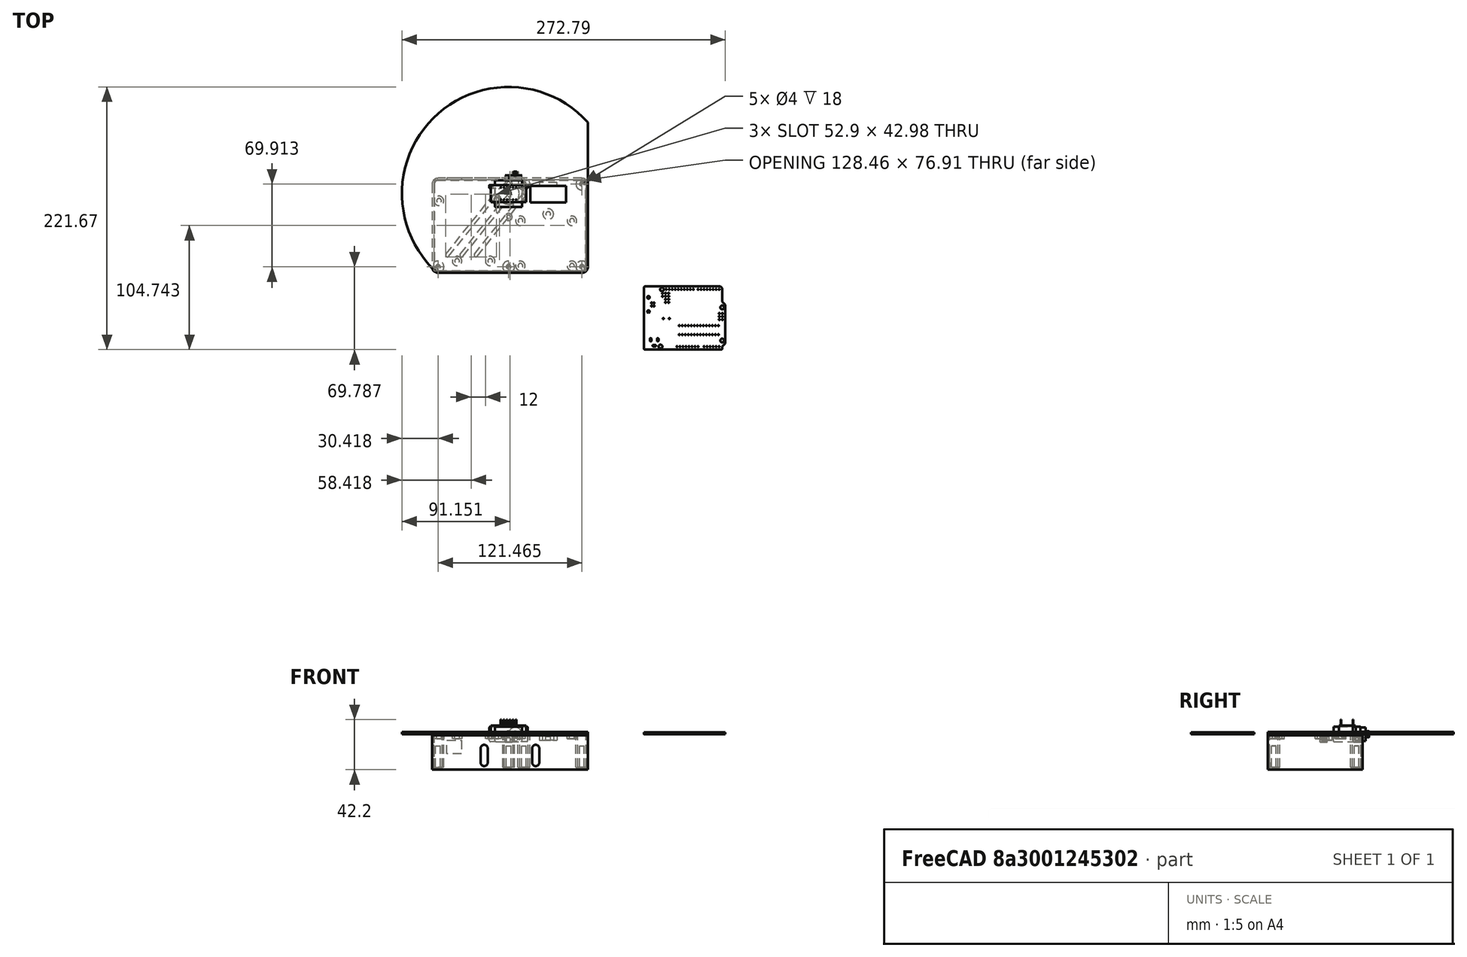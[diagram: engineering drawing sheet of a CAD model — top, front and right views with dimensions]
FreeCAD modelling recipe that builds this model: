
FCSTD DOCUMENT  (FreeCAD 1.0RUnknown)
Label: shell
License: All rights reserved
LicenseURL: https://en.wikipedia.org/wiki/All_rights_reserved
objects: Sketcher::SketchObject×12, PartDesign::Pad×9, PartDesign::Pocket×5, PartDesign::Hole×5, App::Link×4, App::FeaturePython×4, Part::Feature×3, PartDesign::SubShapeBinder×2, PartDesign::Body×2, App::Part×1, Assembly::JointGroup×1, Assembly::AssemblyObject×1, PartDesign::Chamfer×1
note: 91 computed .brp shape members not serialized (recipe doc carries the construction recipe); baked Part::Feature solids carry a one-line shape summary decoded from their .brp

FEATURE [Sketcher::SketchObject] Sketch
  ArcFitTolerance = 1e-06
  AttachmentSupport = -> [XY_Plane]
  FullyConstrained = true
  MakeInternals = false
  MapMode = 5
  sketch-geometry (14):
    g0: LineSegment StartX=18.4415 StartY=6.5 StartZ=0 EndX=18.4415 EndY=-7.5 EndZ=0
    g1: LineSegment StartX=18.4415 StartY=-7.5 StartZ=0 EndX=48.4415 EndY=-7.5 EndZ=0
    g2: LineSegment StartX=48.4415 StartY=-7.5 StartZ=0 EndX=48.4415 EndY=6.5 EndZ=0
    g3: LineSegment StartX=48.4415 StartY=6.5 StartZ=0 EndX=18.4415 EndY=6.5 EndZ=0
    g4: GeomPoint [constr] X=33.4415 Y=-0.5 Z=0
    g5: ArcOfCircle CenterX=0 CenterY=0 CenterZ=0 NormalX=0 NormalY=0 NormalZ=1 AngleXU=0 Radius=90 StartAngle=0.733038 EndAngle=3.97935
    g6: Circle CenterX=0 CenterY=0 CenterZ=0 NormalX=0 NormalY=0 NormalZ=1 AngleXU=0 Radius=2.5
    g7: LineSegment [constr] StartX=0 StartY=0 StartZ=0 EndX=66.883 EndY=60.2218 EndZ=0
    g8: LineSegment [constr] StartX=0 StartY=0 StartZ=0 EndX=-60.2218 EndY=-66.883 EndZ=0
    g9: LineSegment StartX=66.883 StartY=60.2218 StartZ=0 EndX=66.883 EndY=-61.883 EndZ=0
    g10: LineSegment StartX=61.883 StartY=-66.883 StartZ=0 EndX=-60.2218 EndY=-66.883 EndZ=0
    g11: ArcOfCircle CenterX=61.883 CenterY=-61.883 CenterZ=0 NormalX=0 NormalY=0 NormalZ=1 AngleXU=0 Radius=5 StartAngle=4.71239 EndAngle=6.28319
    g12: LineSegment [constr] StartX=48.4415 StartY=3.78 StartZ=0 EndX=66.883 EndY=3.78 EndZ=0
    g13: LineSegment [constr] StartX=0 StartY=0 StartZ=0 EndX=18.4415 EndY=0 EndZ=0
  constraints (37):
    c: Coincident(g0,g1)
    c: Coincident(g1,g2)
    c: Coincident(g2,g3)
    c: Coincident(g3,g0)
    c: Vertical(g2)
    c: Horizontal(g1)
    c: Horizontal(g3)
    c: Symmetric(g2,g0,g4)
    c: DistanceX(g1,g1) = 30
    c: DistanceY(g2,g2) = 14
    c: Radius(g5) = 90
    c: Coincident(g5,g-1)
    c: Coincident(g6,g5)
    c: Diameter(g6) = 5
    c: Coincident(g7,g5)
    c: Coincident(g8,g5)
    c: Angle(g8,g-1,g5) = 2.30383
    c: Vertical(g9)
    c: Horizontal(g10)
    c: Angle(g-1,g7) = 0.733038
    c: Tangent(g9,g11) = 1.5708
    c: Tangent(g10,g11) = 1.5708
    c: Radius(g11) = 5
    c: Coincident(g5,g8)
    c: Coincident(g5,g7)
    c: Coincident(g9,g5)
    c: Coincident(g10,g5)
    c: PointOnObject(g12,g9)
    c: PointOnObject(g12,g2)
    c: DistanceY(g-1,g12) = 3.78
    c: Horizontal(g12,g12)
    c: Coincident(g13,g5)
    c: Vertical(g13,g0)
    c: PointOnObject(g13,g-1)
    c: Equal(g12,g13)
    c: Perpendicular(g0,g1)
    c: DistanceY(g-1,g4) = -0.5
FEATURE [PartDesign::Pad] Pad  label="BaseFace"
  Direction = (0,0,1)
  Length = 2
  Length2 = 10
  Profile = -> Sketch
  ReferenceAxis = -> Sketch [N_Axis]
  Refine = true
  Suppressed = false
  Type = 0
FEATURE [Sketcher::SketchObject] Sketch001
  ArcFitTolerance = 1e-06
  AttachmentSupport = -> [XY_Plane]
  FullyConstrained = true
  MakeInternals = false
  MapMode = 2
  sketch-geometry (1):
    g0: Circle CenterX=0 CenterY=0 CenterZ=0 NormalX=0 NormalY=0 NormalZ=1 AngleXU=0 Radius=9
  constraints (2):
    c: Diameter(g0) = 18
    c: Coincident(g0,g-1)
FEATURE [Sketcher::SketchObject] Sketch003
  ArcFitTolerance = 1e-06
  AttachmentOffset = pos=(0,0,2) rot=(0,0,1;0rad)
  AttachmentSupport = -> [XY_Plane]
  FullyConstrained = true
  MakeInternals = false
  MapMode = 5
  Placement = pos=(0,0,2) rot=(0,0,1;0rad)
  expr: .AttachmentOffset.Base.z = <<BaseFace>>.Length
  sketch-geometry (3):
    g0: Circle CenterX=0 CenterY=-19.72 CenterZ=0 NormalX=0 NormalY=0 NormalZ=1 AngleXU=0 Radius=3
    g1: Circle CenterX=0 CenterY=8.53 CenterZ=0 NormalX=0 NormalY=0 NormalZ=1 AngleXU=0 Radius=3
    g2: LineSegment [constr] StartX=0 StartY=-19.72 StartZ=0 EndX=0 EndY=8.53 EndZ=0
  constraints (8):
    c: Diameter(g0) = 6
    c: Diameter(g1) = 6
    c: Distance(g0,g1) = 28.25
    c: Distance(g1,g-1) = 8.53
    c: Coincident(g2,g0)
    c: Coincident(g2,g1)
    c: PointOnObject(g-1,g2)
    c: PointOnObject(g0,g-2)
FEATURE [PartDesign::Pocket] Pocket001  label="PocketServo"
  BaseFeature = -> Pad
  Direction = (0,0,-1)
  Length = 1.5
  Length2 = 5
  Profile = -> Sketch001
  ReferenceAxis = -> Sketch001 [N_Axis]
  Refine = true
  Reversed = true
  Suppressed = false
  Type = 0
FEATURE [Sketcher::SketchObject] Sketch002
  ArcFitTolerance = 1e-06
  AttachmentSupport = -> [XY_Plane]
  ExternalGeometry = -> [Pocket001]
  FullyConstrained = true
  MakeInternals = false
  MapMode = 5
  sketch-geometry (5):
    g0: Circle CenterX=-43.4418 CenterY=-56.923 CenterZ=0 NormalX=0 NormalY=0 NormalZ=1 AngleXU=0 Radius=4
    g1: Circle CenterX=-15.5018 CenterY=-56.923 CenterZ=0 NormalX=0 NormalY=0 NormalZ=1 AngleXU=0 Radius=4
    g2: Circle CenterX=-10.4218 CenterY=-4.85303 CenterZ=0 NormalX=0 NormalY=0 NormalZ=1 AngleXU=0 Radius=4
    g3: Circle CenterX=-58.6818 CenterY=-6.12303 CenterZ=0 NormalX=0 NormalY=0 NormalZ=1 AngleXU=0 Radius=4
    g4: GeomPoint X=-61.2218 Y=9.11697 Z=0
  constraints (14):
    c: Equal(g1,g0)
    c: Equal(g0,g3)
    c: Equal(g3,g2)
    c: Diameter(g3) = 8
    c: DistanceY(g4,g3) = -15.24
    c: DistanceY(g4,g0) = -66.04
    c: Horizontal(g0,g1)
    c: DistanceX(g4,g3) = 2.54
    c: DistanceX(g4,g2) = 50.8
    c: DistanceX(g4,g0) = 17.78
    c: DistanceX(g4,g1) = 45.72
    c: DistanceX(g4,g-3) = 1
    c: DistanceY(g4,g-3) = -76
    c: DistanceY(g4,g2) = -13.97
FEATURE [PartDesign::Pad] Pad005  label="PadArduino"
  BaseFeature = -> Pocket001
  Direction = (0,0,1)
  Length = 4
  Length2 = 10
  Profile = -> Sketch002
  ReferenceAxis = -> Sketch002 [N_Axis]
  Refine = true
  Reversed = true
  Suppressed = false
  Type = 0
FEATURE [PartDesign::Pad] Pad002  label="PadServo"
  BaseFeature = -> Pad005
  Direction = (0,0,1)
  Length = 8.75
  Length2 = 10
  Profile = -> Sketch003
  ReferenceAxis = -> Sketch003 [N_Axis]
  Refine = true
  Reversed = true
  Suppressed = false
  Type = 0
  expr: Length = 6.75 mm + <<BaseFace>>.Length
FEATURE [Sketcher::SketchObject] Sketch004
  ArcFitTolerance = 1e-06
  AttachmentSupport = -> [XY_Plane003]
  ExternalGeometry = -> [Pad002]
  FullyConstrained = true
  MakeInternals = false
  MapMode = 5
  sketch-geometry (16):
    g0: LineSegment StartX=61.883 StartY=11.53 StartZ=0 EndX=-59.5818 EndY=11.53 EndZ=0
    g1: LineSegment StartX=-63.0818 StartY=8.03 StartZ=0 EndX=-63.0818 EndY=-61.883 EndZ=0
    g2: LineSegment StartX=-59.5818 StartY=-65.383 StartZ=0 EndX=61.883 EndY=-65.383 EndZ=0
    g3: LineSegment StartX=65.383 StartY=-61.883 StartZ=0 EndX=65.383 EndY=8.03 EndZ=0
    g4: ArcOfCircle CenterX=61.883 CenterY=8.03 CenterZ=0 NormalX=0 NormalY=0 NormalZ=1 AngleXU=0 Radius=3.5 StartAngle=1e-16 EndAngle=1.5708
    g5: ArcOfCircle CenterX=-59.5818 CenterY=8.03 CenterZ=0 NormalX=0 NormalY=0 NormalZ=1 AngleXU=0 Radius=3.5 StartAngle=1.5708 EndAngle=3.14159
    g6: ArcOfCircle CenterX=-59.5818 CenterY=-61.883 CenterZ=0 NormalX=0 NormalY=0 NormalZ=1 AngleXU=0 Radius=3.5 StartAngle=3.14159 EndAngle=4.71239
    g7: ArcOfCircle CenterX=61.883 CenterY=-61.883 CenterZ=0 NormalX=0 NormalY=0 NormalZ=1 AngleXU=0 Radius=3.5 StartAngle=4.71239 EndAngle=6.28319
    g8: LineSegment StartX=61.883 StartY=13.03 StartZ=0 EndX=-59.5818 EndY=13.03 EndZ=0
    g9: LineSegment StartX=-64.5818 StartY=8.03 StartZ=0 EndX=-64.5818 EndY=-61.883 EndZ=0
    g10: LineSegment StartX=-59.5818 StartY=-66.883 StartZ=0 EndX=61.883 EndY=-66.883 EndZ=0
    g11: LineSegment StartX=66.883 StartY=-61.883 StartZ=0 EndX=66.883 EndY=8.03 EndZ=0
    g12: ArcOfCircle CenterX=61.883 CenterY=8.03 CenterZ=0 NormalX=0 NormalY=0 NormalZ=1 AngleXU=0 Radius=5 StartAngle=0 EndAngle=1.5708
    g13: ArcOfCircle CenterX=-59.5818 CenterY=8.03 CenterZ=0 NormalX=0 NormalY=0 NormalZ=1 AngleXU=0 Radius=5 StartAngle=1.5708 EndAngle=3.14159
    g14: ArcOfCircle CenterX=-59.5818 CenterY=-61.883 CenterZ=0 NormalX=0 NormalY=0 NormalZ=1 AngleXU=0 Radius=5 StartAngle=3.14159 EndAngle=4.71239
    g15: ArcOfCircle CenterX=61.883 CenterY=-61.883 CenterZ=0 NormalX=0 NormalY=0 NormalZ=1 AngleXU=0 Radius=5 StartAngle=4.71239 EndAngle=6.28319
  constraints (38):
    c: Tangent(g0,g4) = -1.5708
    c: Tangent(g0,g5) = -1.5708
    c: Tangent(g1,g5) = -1.5708
    c: Tangent(g1,g6) = -1.5708
    c: Tangent(g2,g6) = -1.5708
    c: Tangent(g2,g7) = -1.5708
    c: Tangent(g3,g7) = -1.5708
    c: Tangent(g3,g4) = -1.5708
    c: Horizontal(g0)
    c: Horizontal(g2)
    c: Vertical(g1)
    c: Vertical(g3)
    c: Equal(g4,g5)
    c: Equal(g5,g6)
    c: Equal(g6,g7)
    c: Tangent(g8,g12) = -1.5708
    c: Tangent(g8,g13) = -1.5708
    c: Tangent(g9,g13) = -1.5708
    c: Tangent(g9,g14) = -1.5708
    c: Tangent(g10,g14) = -1.5708
    c: Tangent(g10,g15) = -1.5708
    c: Tangent(g11,g15) = -1.5708
    c: Tangent(g11,g12) = -1.5708
    c: Horizontal(g8)
    c: Vertical(g9)
    c: Equal(g12,g13)
    c: Equal(g13,g14)
    c: Equal(g14,g15)
    c: Distance(g10,g2) = 1.5
    c: Vertical(g0,g8)
    c: Horizontal(g3,g11)
    c: Vertical(g8,g0)
    c: Distance(g0,g8) = 1.5
    c: Tangent(g11,g-6)
    c: Distance(g5,g13) = 5
    c: Tangent(g-5,g10)
    c: Tangent(g0,g-3)
    c: Distance(g-4,g1) = 0.4
FEATURE [PartDesign::Pad] Pad006  label="PadContour"
  BaseFeature = -> Pad002
  Direction = (0,0,1)
  Length = 30
  Length2 = 10
  Profile = -> Sketch004
  ReferenceAxis = -> Sketch004 [N_Axis]
  Refine = true
  Reversed = true
  Suppressed = false
  Type = 0
FEATURE [Sketcher::SketchObject] Sketch005
  ArcFitTolerance = 1e-06
  ExternalGeometry = -> [Sketch002]
  FullyConstrained = true
  MakeInternals = false
  MapMode = 5
  Placement = pos=(0,12.03,0) rot=(0,0.707107,0.707107;3.14159rad)
  sketch-geometry (4):
    g0: LineSegment StartX=52.1718 StartY=-16.66 StartZ=0 EndX=52.1718 EndY=-5.26 EndZ=0
    g1: LineSegment StartX=52.1718 StartY=-5.26 StartZ=0 EndX=39.6718 EndY=-5.26 EndZ=0
    g2: LineSegment StartX=39.6718 StartY=-5.26 StartZ=0 EndX=39.6718 EndY=-16.66 EndZ=0
    g3: LineSegment StartX=39.6718 StartY=-16.66 StartZ=0 EndX=52.1718 EndY=-16.66 EndZ=0
  constraints (12):
    c: Coincident(g0,g1)
    c: Coincident(g1,g2)
    c: Coincident(g2,g3)
    c: Coincident(g3,g0)
    c: Vertical(g0)
    c: Vertical(g2)
    c: Horizontal(g1)
    c: Horizontal(g3)
    c: DistanceY(g1,g-3) = 5.26
    c: DistanceX(g0,g-3) = 9.05
    c: DistanceX(g1,g1) = 12.5
    c: DistanceY(g2,g2) = 11.4
FEATURE [PartDesign::Pocket] Pocket  label="PocketUSB"
  BaseFeature = -> Pad006
  Direction = (-1e-16,-1,2e-16)
  Length = 5
  Length2 = 5
  Profile = -> Sketch005
  ReferenceAxis = -> Sketch005 [N_Axis]
  Refine = true
  Reversed = true
  Suppressed = false
  Type = 4
FEATURE [Sketcher::SketchObject] Sketch006
  ArcFitTolerance = 1e-06
  AttachmentSupport = -> [XY_Plane]
  ExternalGeometry = -> [Pocket]
  FullyConstrained = true
  MakeInternals = false
  MapMode = 5
  sketch-geometry (6):
    g0: Circle CenterX=33.4415 CenterY=-17.25 CenterZ=0 NormalX=0 NormalY=0 NormalZ=1 AngleXU=0 Radius=4.5
    g1: LineSegment StartX=40.9415 StartY=9.3 StartZ=0 EndX=25.9415 EndY=9.3 EndZ=0
    g2: LineSegment StartX=25.9415 StartY=9.3 StartZ=0 EndX=25.9415 EndY=6.5 EndZ=0
    g3: LineSegment StartX=25.9415 StartY=6.5 StartZ=0 EndX=40.9415 EndY=6.5 EndZ=0
    g4: LineSegment StartX=40.9415 StartY=6.5 StartZ=0 EndX=40.9415 EndY=9.3 EndZ=0
    g5: GeomPoint [constr] X=33.4415 Y=7.9 Z=0
  constraints (16):
    c: Diameter(g0) = 9
    c: Distance(g0,g-3) = 23.75
    c: Coincident(g1,g2)
    c: Coincident(g2,g3)
    c: Coincident(g3,g4)
    c: Coincident(g4,g1)
    c: Horizontal(g3)
    c: Vertical(g2)
    c: Vertical(g4)
    c: Symmetric(g3,g1,g5)
    c: PointOnObject(g2,g-3)
    c: DistanceX(g-3,g5) = 15
    c: Equal(g2,g4)
    c: DistanceY(g2,g1) = 2.8
    c: DistanceX(g1,g1) = 15
    c: DistanceX(g-4,g0) = 15
FEATURE [PartDesign::Pad] Pad007
  BaseFeature = -> Pocket
  Direction = (0,0,1)
  Length = 5
  Length2 = 10
  Profile = -> Sketch006
  ReferenceAxis = -> Sketch006 [N_Axis]
  Refine = true
  Reversed = true
  Suppressed = false
  Type = 0
FEATURE [PartDesign::Hole] Hole002  label="HoleDigits"
  BaseFeature = -> Pad007
  CustomThreadClearance = 0
  Depth = 3
  DepthType = 0
  Diameter = 4
  DrillForDepth = false
  DrillPoint = 0
  DrillPointAngle = 118
  HoleCutCountersinkAngle = 90
  HoleCutCustomValues = false
  HoleCutDepth = 0
  HoleCutDiameter = 6.1
  HoleCutType = 0
  ModelThread = false
  Profile = -> Pad007 [Face49]
  Refine = true
  Suppressed = false
  Tapered = false
  TaperedAngle = 90
  ThreadClass = 0
  ThreadDepth = 3
  ThreadDepthType = 0
  ThreadDirection = 0
  ThreadFit = 0
  ThreadSize = 0
  ThreadType = 0
  Threaded = false
  UseCustomThreadClearance = false
FEATURE [App::Link] shell  label="shell001"
  LinkedObject = -> Body
FEATURE [App::FeaturePython] GroundedJoint  # Assembly grounded joint (typed FeaturePython)
  ObjectToGround = -> shell
FEATURE [Part::Feature] Part__Feature  label="SG90-SERVO"
  shape: bbox 32.25 x 29.75 x 12.5 mm, 92 faces (baked)
FEATURE [Part::Feature] Part__Feature001  label="Corps"
  shape: bbox 30 x 14 x 12.2 mm, 30 faces (baked)
FEATURE [Part::Feature] Part__Feature002  label="UNO-TH_Rev3e_PCB"
  shape: bbox 68.58 x 53.34 x 1.51 mm, 119 faces (baked)
FEATURE [App::Part] UNO_TH_Rev3e_1  label="UNO-TH_Rev3e 1"
  Group = -> [Part__Feature002]
  Origin = -> Origin002
FEATURE [App::Link] SG90_SERVO  label="SG90-SERVO001"
  LinkPlacement = pos=(-1.1e-15,-5.595,-14) rot=(0.57735,0.57735,0.57735;2.0944rad)
  LinkedObject = -> Part__Feature
  Placement = pos=(-1.1e-15,-5.595,-14) rot=(0.57735,0.57735,0.57735;2.0944rad)
FEATURE [App::Link] Corps  label="Corps001"
  LinkPlacement = pos=(33.4415,-0.5,0) rot=(1,0,0;3.14159rad)
  LinkedObject = -> Part__Feature001
  Placement = pos=(33.4415,-0.5,0) rot=(1,0,0;3.14159rad)
FEATURE [App::Link] UNO_TH_Rev3e_PCB  label="UNO-TH_Rev3e_PCB001"
  LinkPlacement = pos=(-138.937,123.752,-4) rot=(-0.705895,0.708317,0;3.14159rad)
  LinkedObject = -> Part__Feature002
  Placement = pos=(-138.937,123.752,-4) rot=(-0.705895,0.708317,0;3.14159rad)
FEATURE [App::FeaturePython] Joint002  label="Parallèle"  # Assembly joint (typed FeaturePython)
  Activated = true
  AngleMax = 0
  AngleMin = 0
  Detach1 = false
  Detach2 = false
  Distance = 0
  Distance2 = 0
  EnableAngleMax = false
  EnableAngleMin = false
  EnableLengthMax = false
  EnableLengthMin = false
  JointType = 6 (Parallel)
  LengthMax = 0
  LengthMin = 0
  Placement1 = pos=(16.125,6,3) rot=(0.57735,0.57735,0.57735;2.0944rad)
  Reference1 = -> Assembly [SG90_SERVO.Face24,SG90_SERVO.Face24]
  Reference2 = -> Assembly [shell.?Face21,shell.?Face21]
FEATURE [Sketcher::SketchObject] Sketch007
  ArcFitTolerance = 1e-06
  FullyConstrained = true
  MakeInternals = false
  Placement = pos=(0,0,0) rot=(1,0,0;3.14159rad)
  sketch-geometry (7):
    g0: Circle CenterX=53.5 CenterY=61 CenterZ=0 NormalX=0 NormalY=0 NormalZ=1 AngleXU=0 Radius=4
    g1: Circle CenterX=10 CenterY=23 CenterZ=0 NormalX=0 NormalY=0 NormalZ=1 AngleXU=0 Radius=4
    g2: Circle CenterX=53.5 CenterY=23 CenterZ=0 NormalX=0 NormalY=0 NormalZ=1 AngleXU=0 Radius=4
    g3: Circle CenterX=10 CenterY=61 CenterZ=0 NormalX=0 NormalY=0 NormalZ=1 AngleXU=0 Radius=4
    g4: LineSegment [constr] StartX=10 StartY=61 StartZ=0 EndX=53.5 EndY=61 EndZ=0
    g5: LineSegment [constr] StartX=10 StartY=23 StartZ=0 EndX=53.5 EndY=23 EndZ=0
    g6: LineSegment [constr] StartX=53.5 StartY=23 StartZ=0 EndX=53.5 EndY=61 EndZ=0
  constraints (18):
    c: Equal(g3,g0)
    c: Equal(g0,g2)
    c: Equal(g2,g1)
    c: Diameter(g3) = 8
    c: Coincident(g4,g3)
    c: Coincident(g4,g0)
    c: Coincident(g5,g1)
    c: Coincident(g5,g2)
    c: Coincident(g6,g2)
    c: Coincident(g6,g0)
    c: Vertical(g6)
    c: Horizontal(g4)
    c: Horizontal(g5)
    c: Equal(g5,g4)
    c: DistanceX(g4,g4) = 43.5
    c: DistanceY(g6,g6) = 38
    c: DistanceY(g-1,g1) = 23
    c: DistanceX(g-1,g1) = 10
FEATURE [PartDesign::Pad] Pad008
  BaseFeature = -> Hole002
  Direction = (0,-1e-16,-1)
  Length = 4
  Length2 = 10
  Profile = -> Sketch007
  ReferenceAxis = -> Sketch007 [N_Axis]
  Refine = true
  Suppressed = false
  Type = 0
FEATURE [PartDesign::Hole] Hole  label="HoleMainBoard"
  BaseFeature = -> Pad008
  CustomThreadClearance = 0
  Depth = 4
  DepthType = 0
  Diameter = 4
  DrillForDepth = false
  DrillPoint = 0
  DrillPointAngle = 118
  HoleCutCountersinkAngle = 90
  HoleCutCustomValues = false
  HoleCutDepth = 0
  HoleCutDiameter = 6.1
  HoleCutType = 0
  ModelThread = false
  Profile = -> Pad008 [Face53,Face61,Face58,Face52]
  Refine = true
  Suppressed = false
  Tapered = false
  TaperedAngle = 90
  ThreadClass = 0
  ThreadDepth = 4
  ThreadDepthType = 0
  ThreadDirection = 0
  ThreadFit = 0
  ThreadSize = 0
  ThreadType = 0
  Threaded = false
  UseCustomThreadClearance = false
FEATURE [PartDesign::Hole] Hole003  label="HoleUNO"
  BaseFeature = -> Hole
  CustomThreadClearance = 0
  Depth = 4
  DepthType = 0
  Diameter = 4
  DrillForDepth = false
  DrillPoint = 0
  DrillPointAngle = 118
  HoleCutCountersinkAngle = 90
  HoleCutCustomValues = false
  HoleCutDepth = 0
  HoleCutDiameter = 6.1
  HoleCutType = 0
  ModelThread = false
  Profile = -> Hole [Face54,Face50,Face51,Face57]
  Refine = true
  Suppressed = false
  Tapered = false
  TaperedAngle = 90
  ThreadClass = 0
  ThreadDepth = 4
  ThreadDepthType = 0
  ThreadDirection = 0
  ThreadFit = 0
  ThreadSize = 0
  ThreadType = 0
  Threaded = false
  UseCustomThreadClearance = false
FEATURE [Sketcher::SketchObject] Sketch008
  ArcFitTolerance = 1e-06
  AttachmentSupport = -> [XY_Plane]
  ExternalGeometry = -> [Hole003]
  FullyConstrained = true
  MakeInternals = false
  MapMode = 5
  Placement = pos=(0,0,0) rot=(0,1,0;3.14159rad)
  sketch-geometry (5):
    g0: Circle CenterX=-61.883 CenterY=8.03 CenterZ=0 NormalX=0 NormalY=0 NormalZ=1 AngleXU=0 Radius=5
    g1: Circle CenterX=59.5818 CenterY=-61.883 CenterZ=0 NormalX=0 NormalY=0 NormalZ=1 AngleXU=0 Radius=5
    g2: Circle CenterX=-61.883 CenterY=-61.883 CenterZ=0 NormalX=0 NormalY=0 NormalZ=1 AngleXU=0 Radius=5
    g3: Circle CenterX=0 CenterY=-61.883 CenterZ=0 NormalX=0 NormalY=0 NormalZ=1 AngleXU=0 Radius=5
    g4: Circle CenterX=-13 CenterY=8.03 CenterZ=0 NormalX=0 NormalY=0 NormalZ=1 AngleXU=0 Radius=5
  constraints (15):
    c: Equal(g2,g3)
    c: Equal(g3,g0)
    c: Diameter(g0) = 10
    c: Tangent(g1,g-6)
    c: Tangent(g0,g-3)
    c: Tangent(g0,g-4)
    c: PointOnObject(g3,g-2)
    c: Tangent(g3,g-5)
    c: Tangent(g2,g-5)
    c: Tangent(g2,g-4)
    c: Diameter(g1) = 10
    c: Tangent(g1,g-5)
    c: Equal(g0,g4)
    c: Tangent(g4,g-3)
    c: Distance(g4,g-2) = 13
FEATURE [PartDesign::Pad] Pad009
  BaseFeature = -> Hole003
  Direction = (0,0,-1)
  Length = 28
  Length2 = 10
  Profile = -> Sketch008
  ReferenceAxis = -> Sketch008 [N_Axis]
  Refine = true
  Suppressed = false
  Type = 0
FEATURE [App::FeaturePython] Joint  label="Pivot"  # Assembly joint (typed FeaturePython)
  Activated = true
  AngleMax = 0
  AngleMin = 0
  Detach1 = false
  Detach2 = false
  Distance = 0
  Distance2 = 0
  EnableAngleMax = false
  EnableAngleMin = false
  EnableLengthMax = false
  EnableLengthMin = false
  JointType = 1 (Revolute)
  LengthMax = 0
  LengthMin = 0
  Offset2 = pos=(0,0,1.51) rot=(0,0,1;0rad)
  Placement1 = pos=(180.251,-124.054,1.51) rot=(0.707107,-0.707107,0;3.14159rad)
  Placement2 = pos=(-15.5018,-56.923,-5.51) rot=(0,1,0;3.14159rad)
  Reference1 = -> Assembly [UNO_TH_Rev3e_PCB.Edge183,UNO_TH_Rev3e_PCB.Edge183]
  Reference2 = -> Assembly [shell.Edge232,shell.Edge232]
FEATURE [PartDesign::Hole] Hole004
  BaseFeature = -> Pad009
  CustomThreadClearance = 0
  Depth = 4
  DepthType = 0
  Diameter = 3.2
  DrillForDepth = false
  DrillPoint = 0
  DrillPointAngle = 118
  HoleCutCountersinkAngle = 90
  HoleCutCustomValues = false
  HoleCutDepth = 0
  HoleCutDiameter = 6.1
  HoleCutType = 0
  ModelThread = false
  Profile = -> Pad002 [Face19,Face22]
  Refine = true
  Suppressed = false
  Tapered = false
  TaperedAngle = 90
  ThreadClass = 0
  ThreadDepth = 4
  ThreadDepthType = 0
  ThreadDirection = 0
  ThreadFit = 0
  ThreadSize = 0
  ThreadType = 0
  Threaded = false
  UseCustomThreadClearance = false
FEATURE [App::FeaturePython] Joint003  label="Pivot001"  # Assembly joint (typed FeaturePython)
  Activated = true
  AngleMax = 0
  AngleMin = 0
  Detach1 = false
  Detach2 = false
  Distance = 0
  Distance2 = 0
  EnableAngleMax = false
  EnableAngleMin = false
  EnableLengthMax = false
  EnableLengthMin = false
  JointType = 1 (Revolute)
  LengthMax = 0
  LengthMin = 0
  Offset2 = pos=(0,0,2.5) rot=(0,0,1;0rad)
  Placement1 = pos=(-14.125,4.75,0) rot=(-0.186157,-0.694747,-0.694747;2.77349rad)
  Placement2 = pos=(0,-19.72,-9.25) rot=(0,1,0;3.14159rad)
  Reference1 = -> Assembly [SG90_SERVO.Edge57,SG90_SERVO.Edge57]
  Reference2 = -> Assembly [shell.Edge238,shell.Edge238]
FEATURE [Assembly::JointGroup] Joints
  Group = -> [GroundedJoint,Joint002,Joint,Joint003]
FEATURE [Assembly::AssemblyObject] Assembly
  Group = -> [Joints,shell,GroundedJoint,SG90_SERVO,Corps,UNO_TH_Rev3e_PCB,Joint002,Joint,Joint003]
  Origin = -> Origin001
  Type = Assembly
FEATURE [PartDesign::Hole] Hole005
  BaseFeature = -> Hole004
  CustomThreadClearance = 0
  Depth = 18
  DepthType = 0
  Diameter = 4
  DrillForDepth = false
  DrillPoint = 0
  DrillPointAngle = 118
  HoleCutCountersinkAngle = 90
  HoleCutCustomValues = false
  HoleCutDepth = 0
  HoleCutDiameter = 6.1
  HoleCutType = 0
  ModelThread = false
  Profile = -> Hole004 [Face42,Face44,Face40,Face37,Face46]
  Refine = true
  Suppressed = false
  Tapered = false
  TaperedAngle = 90
  ThreadClass = 0
  ThreadDepth = 18
  ThreadDepthType = 0
  ThreadDirection = 0
  ThreadFit = 0
  ThreadSize = 0
  ThreadType = 0
  Threaded = false
  UseCustomThreadClearance = false
FEATURE [PartDesign::SubShapeBinder] Binder
  BindCopyOnChange = 0
  BindMode = 0
  ClaimChildren = false
  Context = -> Body001 [Binder.]
  Fuse = false
  MakeFace = true
  OffsetFill = false
  OffsetIntersection = false
  OffsetJoinType = 0
  OffsetOpenResult = false
  PartialLoad = false
  Refine = true
  Relative = true
  Support = -> [Body[Sketch004.]]
  _Version = 2
FEATURE [PartDesign::Pad] Pad010
  Direction = (0,0,1)
  Length = 1
  Length2 = 10
  Profile = -> Binder [Edge5,Edge6,Edge7,Edge8,Edge1,Edge2,Edge3,Edge4]
  Refine = true
  Reversed = true
  Suppressed = false
  Type = 0
FEATURE [PartDesign::Pad] Pad011
  BaseFeature = -> Pad010
  Direction = (0,0,1)
  Length = 1
  Length2 = 10
  Profile = -> Binder [Edge14,Edge13,Edge15,Edge11,Edge10,Edge12,Edge9,Edge16]
  Refine = true
  Suppressed = false
  Type = 0
FEATURE [PartDesign::Chamfer] Chamfer
  Angle = 45
  Base = -> Pad011 [Edge37,Edge35,Edge48,Edge47,Edge45,Edge43,Edge39,Edge41]
  BaseFeature = -> Pad011
  ChamferType = 1
  FlipDirection = false
  Refine = true
  Size = 0.99
  Size2 = 0.5
  SupportTransform = false
  Suppressed = false
  UseAllEdges = false
FEATURE [PartDesign::SubShapeBinder] Binder001
  BindCopyOnChange = 0
  BindMode = 0
  ClaimChildren = false
  Context = -> Body001 [Binder001.]
  Fuse = false
  MakeFace = true
  OffsetFill = false
  OffsetIntersection = false
  OffsetJoinType = 0
  OffsetOpenResult = false
  PartialLoad = false
  Refine = true
  Relative = true
  Support = -> [Body[Sketch008.]]
  _Version = 2
FEATURE [Sketcher::SketchObject] Sketch009
  ArcFitTolerance = 1e-06
  AttachmentSupport = -> [XY_Plane003]
  ExternalGeometry = -> [Binder001]
  FullyConstrained = true
  MakeInternals = false
  MapMode = 5
  sketch-geometry (5):
    g0: Circle CenterX=-59.5818 CenterY=-61.883 CenterZ=0 NormalX=0 NormalY=0 NormalZ=1 AngleXU=0 Radius=1.55
    g1: Circle CenterX=0 CenterY=-61.883 CenterZ=0 NormalX=0 NormalY=0 NormalZ=1 AngleXU=0 Radius=1.55
    g2: Circle CenterX=61.883 CenterY=-61.883 CenterZ=0 NormalX=0 NormalY=0 NormalZ=1 AngleXU=0 Radius=1.55
    g3: Circle CenterX=61.883 CenterY=8.03 CenterZ=0 NormalX=0 NormalY=0 NormalZ=1 AngleXU=0 Radius=1.55
    g4: Circle CenterX=13 CenterY=8.03 CenterZ=0 NormalX=0 NormalY=0 NormalZ=1 AngleXU=0 Radius=1.55
  constraints (10):
    c: Coincident(g-7,g0)
    c: Equal(g0,g4)
    c: Equal(g4,g1)
    c: Equal(g1,g3)
    c: Equal(g3,g2)
    c: Diameter(g4) = 3.1
    c: Coincident(g1,g-6)
    c: Coincident(g2,g-5)
    c: Coincident(g3,g-4)
    c: Coincident(g-3,g4)
FEATURE [PartDesign::Pocket] Pocket002
  BaseFeature = -> Chamfer
  Direction = (0,0,-1)
  Length = 5
  Length2 = 5
  Midplane = true
  Profile = -> Sketch009
  ReferenceAxis = -> Sketch009 [N_Axis]
  Refine = true
  Suppressed = false
  Type = 1
FEATURE [Sketcher::SketchObject] Sketch010
  ArcFitTolerance = 1e-06
  AttachmentSupport = -> [Hole005]
  ExternalGeometry = -> [Hole005]
  FullyConstrained = true
  MakeInternals = false
  MapMode = 5
  Placement = pos=(0,-66.883,0) rot=(1,0,0;1.5708rad)
  sketch-geometry (8):
    g0: ArcOfCircle CenterX=22.883 CenterY=-24 CenterZ=0 NormalX=0 NormalY=0 NormalZ=1 AngleXU=0 Radius=3 StartAngle=3.14159 EndAngle=6.28319
    g1: ArcOfCircle CenterX=22.883 CenterY=-12 CenterZ=0 NormalX=0 NormalY=0 NormalZ=1 AngleXU=0 Radius=3 StartAngle=1e-16 EndAngle=3.14159
    g2: LineSegment StartX=19.883 StartY=-24 StartZ=0 EndX=19.883 EndY=-12 EndZ=0
    g3: LineSegment StartX=25.883 StartY=-24 StartZ=0 EndX=25.883 EndY=-12 EndZ=0
    g4: ArcOfCircle CenterX=-20.5818 CenterY=-24 CenterZ=0 NormalX=0 NormalY=0 NormalZ=1 AngleXU=0 Radius=3 StartAngle=3.14159 EndAngle=6.28319
    g5: ArcOfCircle CenterX=-20.5818 CenterY=-12 CenterZ=0 NormalX=0 NormalY=0 NormalZ=1 AngleXU=0 Radius=3 StartAngle=3.35329e-11 EndAngle=3.14159
    g6: LineSegment StartX=-23.5818 StartY=-24 StartZ=0 EndX=-23.5818 EndY=-12 EndZ=0
    g7: LineSegment StartX=-17.5818 StartY=-24 StartZ=0 EndX=-17.5818 EndY=-12 EndZ=0
  constraints (20):
    c: Tangent(g0,g2) = 1.5708
    c: Tangent(g0,g3) = -1.5708
    c: Tangent(g1,g2) = 1.5708
    c: Tangent(g1,g3) = -1.5708
    c: Equal(g0,g1)
    c: Radius(g0) = 3
    c: Vertical(g2)
    c: Tangent(g4,g6) = 1.5708
    c: Tangent(g4,g7) = -1.5708
    c: Tangent(g5,g6) = 1.5708
    c: Tangent(g5,g7) = -1.5708
    c: Equal(g4,g5)
    c: Radius(g4) = 3
    c: Vertical(g6)
    c: Horizontal(g5,g1)
    c: Horizontal(g4,g0)
    c: Distance(g1,g-4) = 39
    c: Distance(g5,g-5) = 39
    c: Distance(g5,g-3) = 14
    c: DistanceY(g7,g7) = 12
FEATURE [PartDesign::Pocket] Pocket003
  BaseFeature = -> Hole005
  Direction = (0,1,-2e-16)
  Length = 5
  Length2 = 5
  Profile = -> Sketch010
  ReferenceAxis = -> Sketch010 [N_Axis]
  Refine = true
  Suppressed = false
  Type = 0
FEATURE [PartDesign::Body] Body  label="shell"
  AllowCompound = false
  Group = -> [Sketch,Pad,Sketch001,Pocket001,Sketch002,Pad005,Pad002,Sketch003,Sketch004,Pad006,Sketch005,Pocket,Sketch006,Pad007,Hole002,Sketch007,Pad008,Hole,Hole003,Sketch008,Pad009,Hole004,Hole005,Sketch010,Pocket003]
  Origin = -> Origin
  Tip = -> Pocket003
FEATURE [Sketcher::SketchObject] Sketch011
  ArcFitTolerance = 1e-06
  AttachmentOffset = pos=(0,0,1) rot=(0,0,1;0rad)
  AttachmentSupport = -> [XY_Plane003]
  ExternalGeometry = -> [Pocket002]
  FullyConstrained = true
  MakeInternals = false
  MapMode = 5
  Placement = pos=(0,0,1) rot=(0,0,1;0rad)
  sketch-geometry (14):
    g0: ArcOfCircle CenterX=-51.5818 CenterY=-51.883 CenterZ=0 NormalX=0 NormalY=0 NormalZ=1 AngleXU=0 Radius=1.5 StartAngle=2.466 EndAngle=5.6076
    g1: ArcOfCircle CenterX=-11.5818 CenterY=-1.97 CenterZ=0 NormalX=0 NormalY=0 NormalZ=1 AngleXU=0 Radius=1.5 StartAngle=5.6076 EndAngle=8.74919
    g2: LineSegment StartX=-52.7523 StartY=-50.945 StartZ=0 EndX=-12.7523 EndY=-1.03196 EndZ=0
    g3: LineSegment StartX=-50.4112 StartY=-52.8211 StartZ=0 EndX=-10.4112 EndY=-2.90804 EndZ=0
    g4: LineSegment [constr] StartX=-53.5818 StartY=-1.97 StartZ=0 EndX=55.883 EndY=-1.97 EndZ=0
    g5: LineSegment [constr] StartX=-53.5818 StartY=-51.883 StartZ=0 EndX=55.883 EndY=-51.883 EndZ=0
    g6: ArcOfCircle CenterX=-39.5818 CenterY=-51.883 CenterZ=0 NormalX=0 NormalY=0 NormalZ=1 AngleXU=0 Radius=1.5 StartAngle=2.466 EndAngle=5.6076
    g7: ArcOfCircle CenterX=0.418245 CenterY=-1.97 CenterZ=0 NormalX=0 NormalY=0 NormalZ=1 AngleXU=0 Radius=1.5 StartAngle=5.6076 EndAngle=8.74919
    g8: LineSegment StartX=-40.7523 StartY=-50.945 StartZ=0 EndX=-0.752261 EndY=-1.03196 EndZ=0
    g9: LineSegment StartX=-38.4112 StartY=-52.8211 StartZ=0 EndX=1.58875 EndY=-2.90804 EndZ=0
    g10: ArcOfCircle CenterX=-27.5818 CenterY=-51.883 CenterZ=0 NormalX=0 NormalY=0 NormalZ=1 AngleXU=0 Radius=1.5 StartAngle=2.466 EndAngle=5.6076
    g11: ArcOfCircle CenterX=12.4182 CenterY=-1.97 CenterZ=0 NormalX=0 NormalY=0 NormalZ=1 AngleXU=0 Radius=1.5 StartAngle=5.6076 EndAngle=8.74919
    g12: LineSegment StartX=-28.7523 StartY=-50.945 StartZ=0 EndX=11.2477 EndY=-1.03196 EndZ=0
    g13: LineSegment StartX=-26.4112 StartY=-52.8211 StartZ=0 EndX=13.5888 EndY=-2.90804 EndZ=0
  constraints (38):
    c: Tangent(g0,g2) = 1.5708
    c: Tangent(g0,g3) = -1.5708
    c: Tangent(g1,g2) = 1.5708
    c: Tangent(g1,g3) = -1.5708
    c: Equal(g0,g1)
    c: Horizontal(g4)
    c: Distance(g-3,g4) = 13
    c: PointOnObject(g1,g4)
    c: Horizontal(g5)
    c: Distance(g-4,g5) = 13
    c: PointOnObject(g0,g5)
    c: DistanceX(g0,g1) = 40
    c: Distance(g2,g3) = 3
    c: DistanceX(g-4,g0) = 8
    c: DistanceX(g-3,g4) = 6
    c: DistanceX(g-4,g5) = 6
    c: DistanceX(g5,g-4) = 6
    c: DistanceX(g4,g-3) = 6
    c: Tangent(g6,g8) = 1.5708
    c: Tangent(g6,g9) = -1.5708
    c: Tangent(g7,g8) = 1.5708
    c: Tangent(g7,g9) = -1.5708
    c: Equal(g6,g7)
    c: PointOnObject(g7,g4)
    c: PointOnObject(g6,g5)
    c: Equal(g7,g1)
    c: DistanceX(g6,g7) = 40
    c: Tangent(g10,g12) = 1.5708
    c: Tangent(g10,g13) = -1.5708
    c: Tangent(g11,g12) = 1.5708
    c: Tangent(g11,g13) = -1.5708
    c: Equal(g10,g11)
    c: DistanceX(g10,g11) = 40
    c: PointOnObject(g10,g5)
    c: PointOnObject(g11,g4)
    c: Equal(g1,g11)
    c: DistanceX(g1,g7) = 12
    c: DistanceX(g7,g11) = 12
FEATURE [PartDesign::Pocket] Pocket004
  BaseFeature = -> Pocket002
  Direction = (0,0,-1)
  Length = 5
  Length2 = 5
  Profile = -> Sketch011
  ReferenceAxis = -> Sketch011 [N_Axis]
  Refine = true
  Suppressed = false
  Type = 0
FEATURE [PartDesign::Body] Body001  label="couvercle"
  AllowCompound = false
  Group = -> [Binder,Pad010,Pad011,Chamfer,Binder001,Sketch009,Pocket002,Sketch011,Pocket004]
  Origin = -> Origin003
  Tip = -> Pocket004
